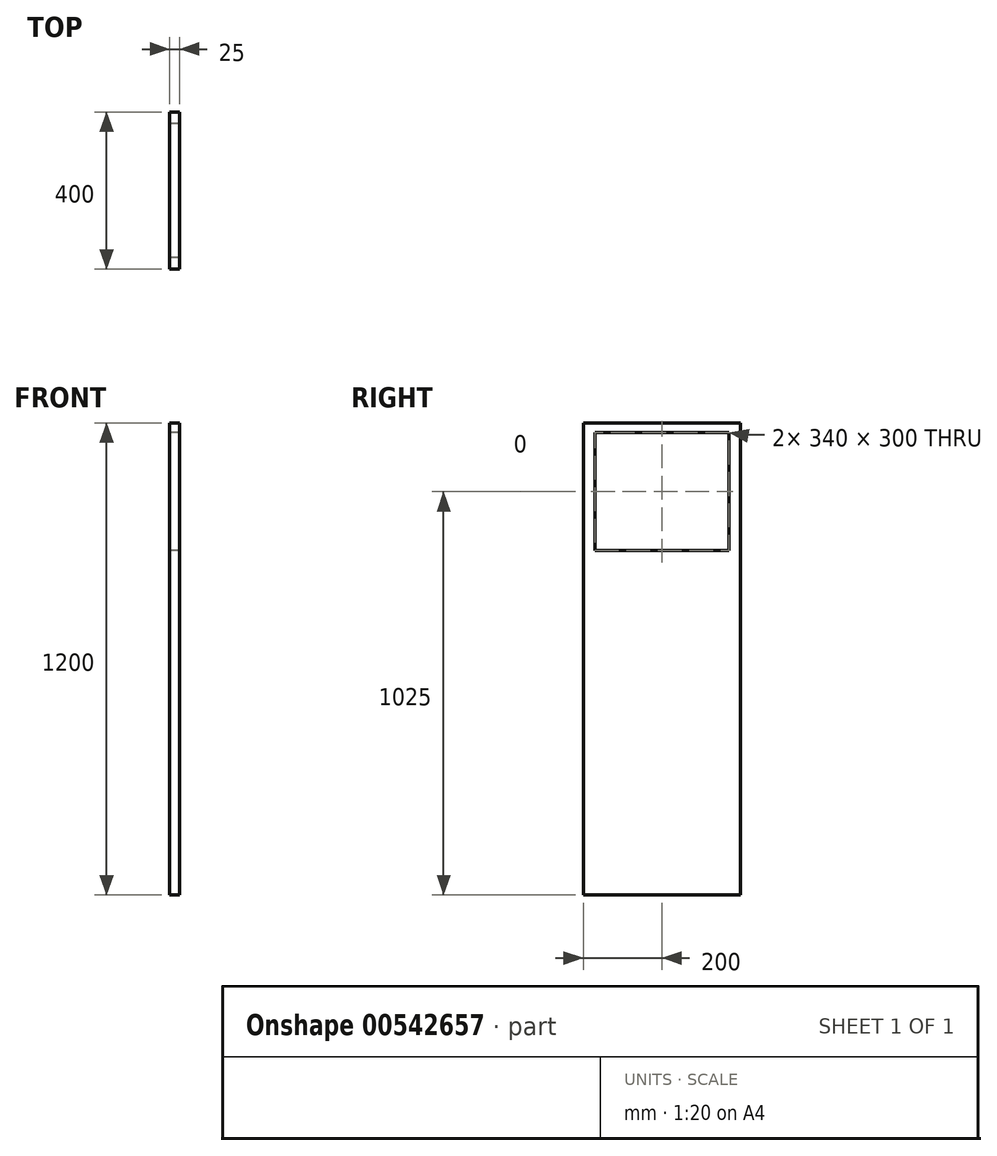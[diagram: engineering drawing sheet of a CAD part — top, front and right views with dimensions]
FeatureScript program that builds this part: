
annotation { "Feature Type Name" : "Feature", "Feature Type Description" : "" }
export const myFeature = defineFeature(function(context is Context, id is Id, definition is map)
    precondition{}
    {
        {
            var Q0;
            Q0=qCreatedBy(makeId("Right.planeOp"),FACE);
            var sketch = newSketch(context, id + "F0", { "sketchPlane" : qUnion([Q0])});
            skLineSegment(sketch, "E0.bottom", {"start": v(0, 0) * mm, "end": v(400, 0) * mm});
            skLineSegment(sketch, "E0.top", {"start": v(0, 1200) * mm, "end": v(400, 1200) * mm});
            skLineSegment(sketch, "E0.left", {"start": v(0, 0) * mm, "end": v(0, 1200) * mm});
            skLineSegment(sketch, "E0.right", {"start": v(400, 0) * mm, "end": v(400, 1200) * mm});
            skLineSegment(sketch, "E1.bottom", {"start": v(30, 1175) * mm, "end": v(370, 1175) * mm});
            skLineSegment(sketch, "E1.top", {"start": v(30, 875) * mm, "end": v(370, 875) * mm});
            skLineSegment(sketch, "E1.left", {"start": v(30, 1175) * mm, "end": v(30, 875) * mm});
            skLineSegment(sketch, "E1.right", {"start": v(370, 1175) * mm, "end": v(370, 875) * mm});
            skSolve(sketch);
        }
        {
            var Q0;
            Q0 = qSketchRegion(id + "F0", true);
            extrude(context, id + "F1", {"entities" : qUnion([Q0]), "depth" : 25 * mm, "offsetDistance" : 25 * mm});
        }
    });
